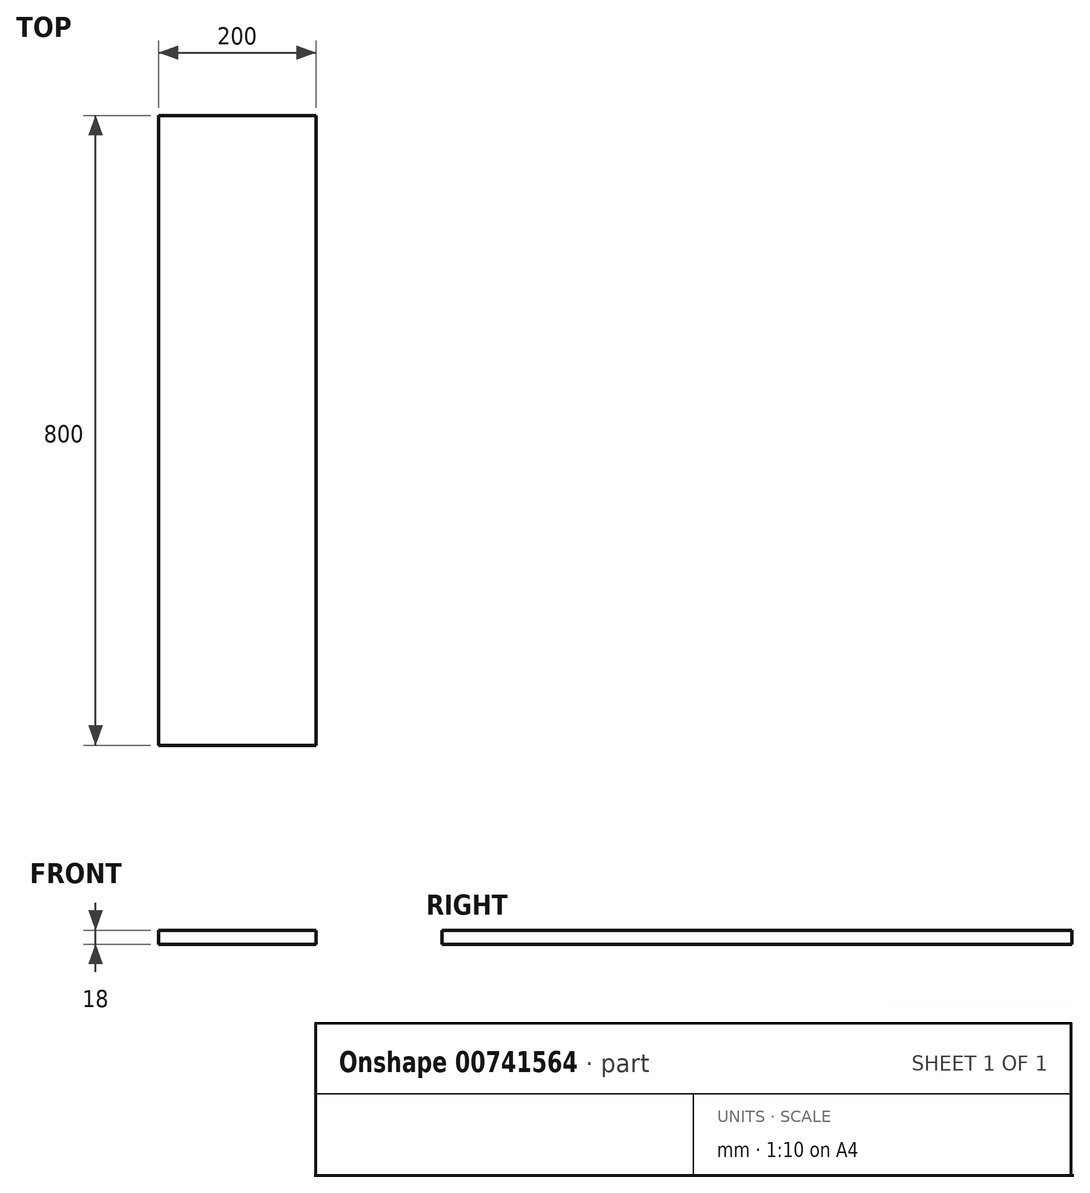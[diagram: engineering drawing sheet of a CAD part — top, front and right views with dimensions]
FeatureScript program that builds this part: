
annotation { "Feature Type Name" : "Feature", "Feature Type Description" : "" }
export const myFeature = defineFeature(function(context is Context, id is Id, definition is map)
    precondition{}
    {
        {
            var Q0;
            Q0=qCreatedBy(makeId("Top.planeOp"),FACE);
            var sketch = newSketch(context, id + "F0", { "sketchPlane" : qUnion([Q0])});
            skLineSegment(sketch, "E0.bottom", {"start": v(-100, -400) * mm, "end": v(100, -400) * mm});
            skLineSegment(sketch, "E0.top", {"start": v(-100, 400) * mm, "end": v(100, 400) * mm});
            skLineSegment(sketch, "E0.left", {"start": v(-100, -400) * mm, "end": v(-100, 400) * mm});
            skLineSegment(sketch, "E0.right", {"start": v(100, -400) * mm, "end": v(100, 400) * mm});
            skPoint(sketch, "E0.middle", {"position": v(0, 0) * mm});
            skSolve(sketch);
        }
        {
            var Q0;
            Q0=qSketchRegion(id+"F0",true);
            extrude(context, id + "F1", {"entities" : qUnion([Q0]), "depth" : 18 * mm, "offsetDistance" : 25 * mm});
        }
    });
